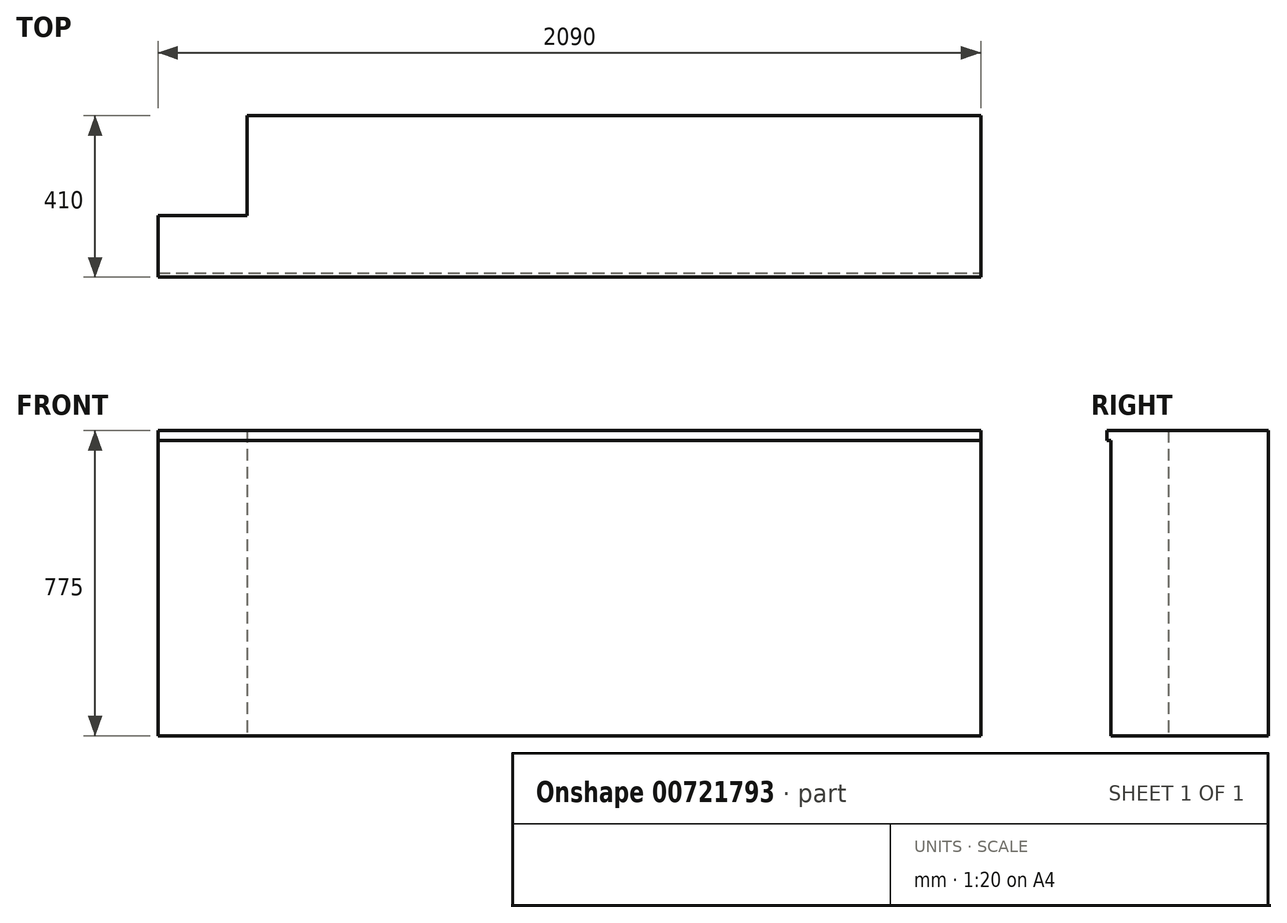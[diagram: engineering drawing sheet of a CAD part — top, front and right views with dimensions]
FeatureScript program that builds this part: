
annotation { "Feature Type Name" : "Feature", "Feature Type Description" : "" }
export const myFeature = defineFeature(function(context is Context, id is Id, definition is map)
    precondition{}
    {
        {
            var Q0;
            Q0=qCreatedBy(makeId("Top.planeOp"),FACE);
            var sketch = newSketch(context, id + "F0", { "sketchPlane" : qUnion([Q0])});
            skLineSegment(sketch, "E0", {"start": v(0, 0) * mm, "end": v(-1864, 0) * mm});
            skLineSegment(sketch, "E1", {"start": v(-1864, 0) * mm, "end": v(-1864, -253) * mm});
            skLineSegment(sketch, "E2", {"start": v(-1864, -253) * mm, "end": v(-2090, -253) * mm});
            skLineSegment(sketch, "E3", {"start": v(-2090, -253) * mm, "end": v(-2090, -400) * mm});
            skLineSegment(sketch, "E4", {"start": v(-2090, -400) * mm, "end": v(0, -400) * mm});
            skLineSegment(sketch, "E5", {"start": v(0, 0) * mm, "end": v(0, -400) * mm});
            skSolve(sketch);
        }
        {
            var Q0;
            Q0=makeQuery(id+"F0.imprint","IMPRINT",FACE,{"disambiguationData":[TD([[makeQuery(id+"F0.imprint","IMPRINT",EDGE,{"derivedFrom":sQuery(id+"F0.wireOp",EDGE,"E0")}),1.0]])]});
            extrude(context, id + "F1", {"entities" : qUnion([Q0]), "depth" : 750 * mm, "offsetDistance" : 25 * mm});
        }
        {
            var Q0;
            Q0=makeQuery(id+"F1.opExtrude","CAP_FACE",FACE,{"disambiguationData":[OSD([sQuery(id+"F0.wireOp",EDGE,"E0"),sQuery(id+"F0.wireOp",EDGE,"E1"),sQuery(id+"F0.wireOp",EDGE,"E2"),sQuery(id+"F0.wireOp",EDGE,"E3"),sQuery(id+"F0.wireOp",EDGE,"E4"),sQuery(id+"F0.wireOp",EDGE,"E5")])],"isStart":false});
            var sketch = newSketch(context, id + "F2", { "sketchPlane" : qUnion([Q0])});
            skLineSegment(sketch, "E6", {"start": v(-1864, 0) * mm, "end": v(-1864, -253) * mm});
            skLineSegment(sketch, "E7", {"start": v(-1864, -253) * mm, "end": v(-2090, -253) * mm});
            skLineSegment(sketch, "E8", {"start": v(-2090, -253) * mm, "end": v(-2090, -400) * mm});
            skLineSegment(sketch, "E9", {"start": v(-2090, -400) * mm, "end": v(-2090, -410) * mm});
            skLineSegment(sketch, "E10", {"start": v(-2090, -410) * mm, "end": v(0, -410) * mm});
            skLineSegment(sketch, "E11", {"start": v(0, -410) * mm, "end": v(0, 0) * mm});
            skLineSegment(sketch, "E12", {"start": v(0, 0) * mm, "end": v(-1864, 0) * mm});
            skSolve(sketch);
        }
        {
            var Q0;
            Q0=makeQuery(id+"F2.imprint","IMPRINT",FACE,{"disambiguationData":[TD([[makeQuery(id+"F2.imprint","IMPRINT",EDGE,{"derivedFrom":sQuery(id+"F2.wireOp",EDGE,"E6")}),1.0]])]});
            var Q1;
            Q1=makeQuery(id+"F2.imprint","IMPRINT",FACE,{"disambiguationData":[TD([[makeQuery(id+"F2.imprint","IMPRINT",EDGE,{"derivedFrom":sQuery(id+"F2.wireOp",EDGE,"E9")}),1.0]])]});
            extrude(context, id + "F3", {"entities" : qUnion([Q0, Q1]), "operationType" : NewBodyOperationType.ADD, "depth" : 25 * mm, "offsetDistance" : 25 * mm});
        }
    });
